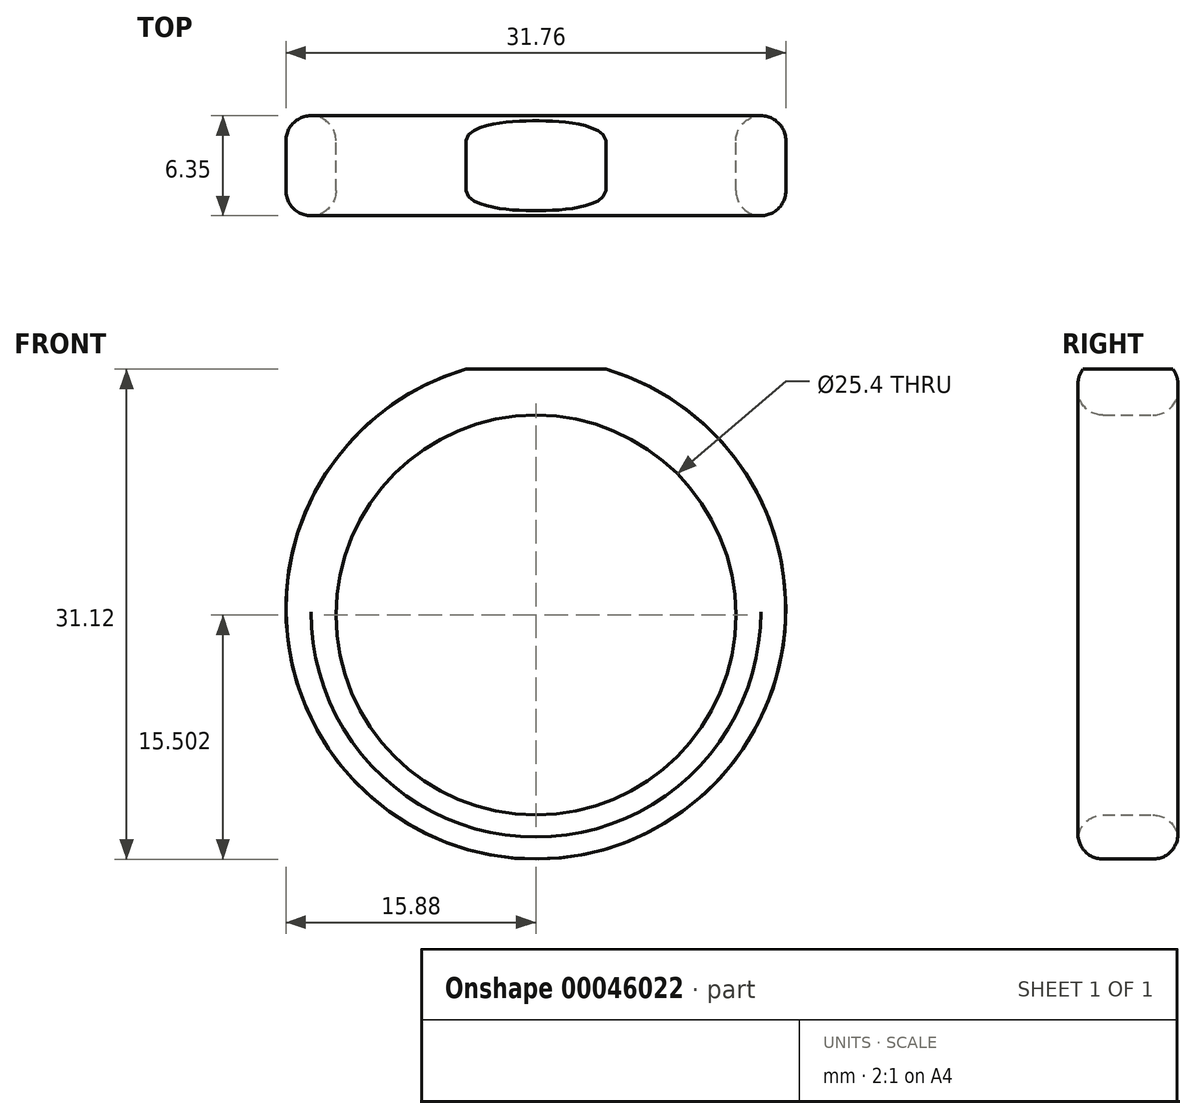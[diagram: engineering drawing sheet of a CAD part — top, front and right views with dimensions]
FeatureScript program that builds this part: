
annotation { "Feature Type Name" : "Feature", "Feature Type Description" : "" }
export const myFeature = defineFeature(function(context is Context, id is Id, definition is map)
    precondition{}
    {
        {
            var Q0;
            Q0=qCreatedBy(makeId("Front.planeOp"),FACE);
            var sketch = newSketch(context, id + "F0", { "sketchPlane" : qUnion([Q0])});
            skArc(sketch, "E0", {"start": v(-4.45, 15.24) * mm, "mid": v(0, -15.88) * mm, "end": v(4.45, 15.24) * mm});
            skCircle(sketch, "E1", {"center": v(0, -0.38) * mm, "radius": 12.7 * mm});
            skLineSegment(sketch, "E2", {"start": v(-4.45, 15.24) * mm, "end": v(4.45, 15.24) * mm});
            skSolve(sketch);
        }
        {
            var Q0;
            Q0=makeQuery(id+"F0.imprint","IMPRINT",FACE,{"disambiguationData":[TD([[makeQuery(id+"F0.imprint","IMPRINT",EDGE,{"derivedFrom":sQuery(id+"F0.wireOp",EDGE,"E0")}),1.0]])]});
            extrude(context, id + "F1", {"entities" : qUnion([Q0]), "depth" : 6.35 * mm});
        }
        {
            var Q0;
            Q0=makeQuery(id+"F1.opExtrude","CAP_EDGE",EDGE,{"disambiguationData":[OSD([sQuery(id+"F0.wireOp",EDGE,"E0")])],"isStart":false});
            var Q1;
            Q1=makeQuery(id+"F1.opExtrude","CAP_EDGE",EDGE,{"disambiguationData":[OSD([sQuery(id+"F0.wireOp",EDGE,"E1")])],"isStart":false});
            var Q2;
            Q2=makeQuery(id+"F1.opExtrude","CAP_EDGE",EDGE,{"disambiguationData":[OSD([sQuery(id+"F0.wireOp",EDGE,"E1")])],"isStart":true});
            var Q3;
            Q3=makeQuery(id+"F1.opExtrude","CAP_EDGE",EDGE,{"disambiguationData":[OSD([sQuery(id+"F0.wireOp",EDGE,"E0")])],"isStart":true});
            fillet(context, id + "F2", {"entities" : qUnion([Q0, Q1, Q2, Q3]), "radius" : 1.59 * mm, "tangentPropagation" : true, "allowEdgeOverflow" : false});
        }
    });
